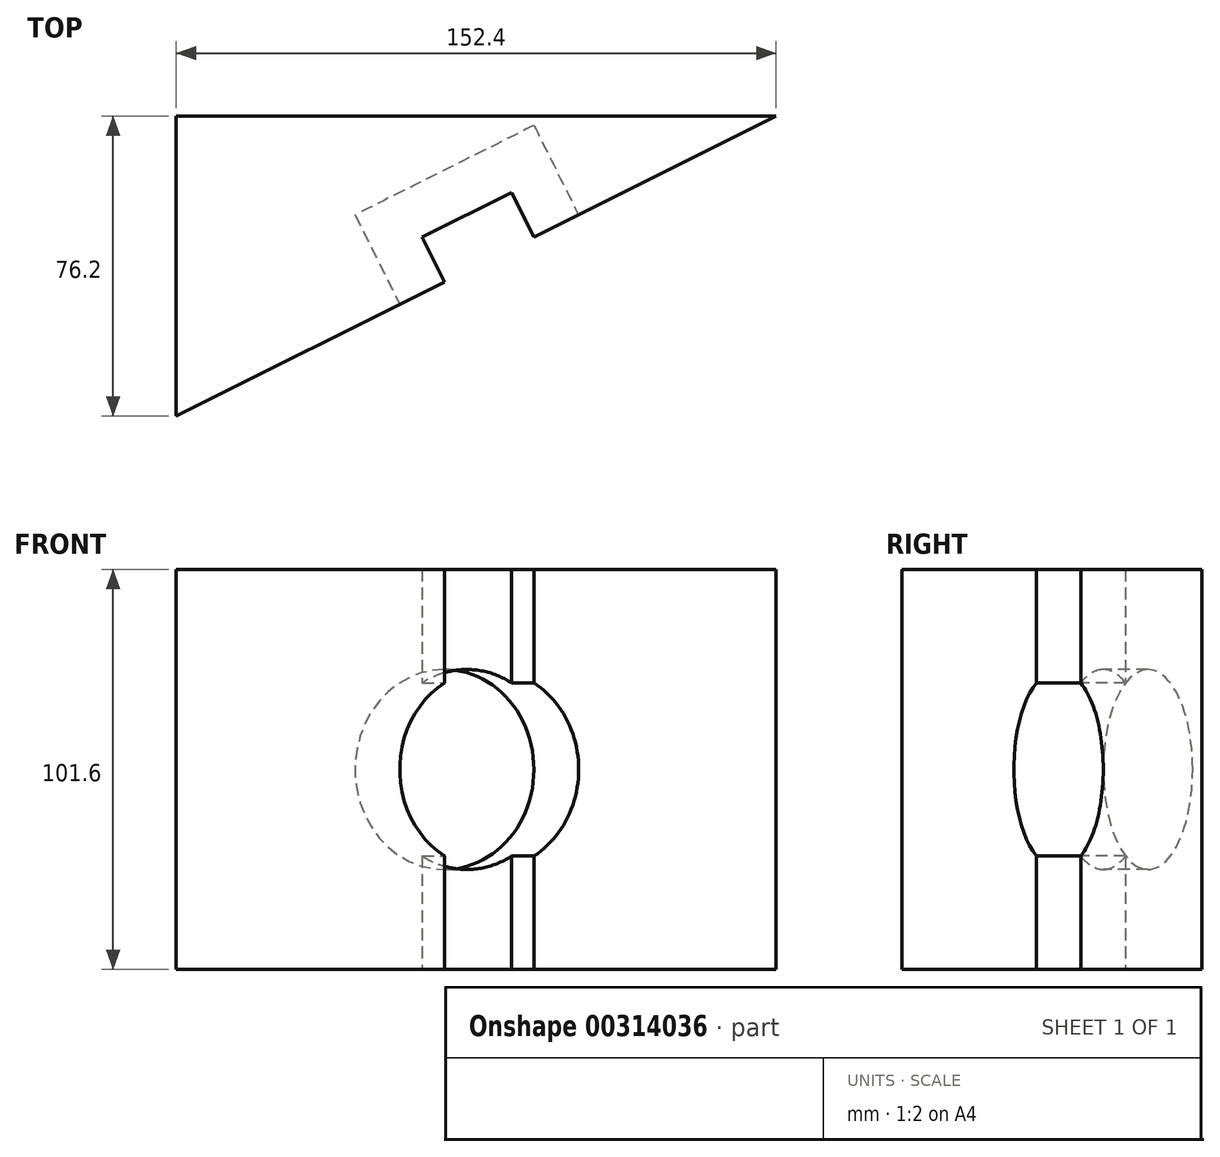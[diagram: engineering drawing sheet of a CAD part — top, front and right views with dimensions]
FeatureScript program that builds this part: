
annotation { "Feature Type Name" : "Feature", "Feature Type Description" : "" }
export const myFeature = defineFeature(function(context is Context, id is Id, definition is map)
    precondition{}
    {
        {
            var Q0;
            Q0=qCreatedBy(makeId("Top.planeOp"),FACE);
            var sketch = newSketch(context, id + "F0", { "sketchPlane" : qUnion([Q0])});
            skLineSegment(sketch, "E0.bottom", {"start": v(0, 0) * mm, "end": v(152.4, 0) * mm});
            skLineSegment(sketch, "E0.top", {"start": v(0, -76.2) * mm, "end": v(152.4, -76.2) * mm});
            skLineSegment(sketch, "E0.left", {"start": v(0, 0) * mm, "end": v(0, -76.2) * mm});
            skLineSegment(sketch, "E0.right", {"start": v(152.4, 0) * mm, "end": v(152.4, -76.2) * mm});
            skLineSegment(sketch, "E1", {"start": v(152.4, 0) * mm, "end": v(0, -76.2) * mm});
            skSolve(sketch);
        }
        {
            var Q0;
            Q0=makeQuery(id+"F0.imprint","IMPRINT",FACE,{"disambiguationData":[TD([[makeQuery(id+"F0.imprint","IMPRINT",EDGE,{"derivedFrom":sQuery(id+"F0.wireOp",EDGE,"E0.bottom")}),-1.0]])]});
            extrude(context, id + "F1", {"entities" : qUnion([Q0]), "depth" : 101.6 * mm});
        }
        {
            var Q0;
            Q0=makeQuery(id+"F1.opExtrude","SWEPT_FACE",FACE,{"disambiguationData":[OSD([sQuery(id+"F0.wireOp",EDGE,"E1")])]});
            var sketch = newSketch(context, id + "F2", { "sketchPlane" : qUnion([Q0])});
            skLineSegment(sketch, "E2.bottom", {"start": v(67.52, 101.6) * mm, "end": v(42.12, 101.6) * mm});
            skLineSegment(sketch, "E2.top", {"start": v(67.52, 0) * mm, "end": v(42.12, 0) * mm});
            skLineSegment(sketch, "E2.left", {"start": v(67.52, 101.6) * mm, "end": v(67.52, 0) * mm});
            skLineSegment(sketch, "E2.right", {"start": v(42.12, 101.6) * mm, "end": v(42.12, 0) * mm});
            skPoint(sketch, "E2.middle", {"position": v(54.82, 50.8) * mm});
            skSolve(sketch);
        }
        {
            var Q0;
            Q0=makeQuery(id+"F2.imprint","IMPRINT",FACE,{"disambiguationData":[TD([[makeQuery(id+"F2.imprint","IMPRINT",EDGE,{"derivedFrom":sQuery(id+"F2.wireOp",EDGE,"E2.bottom")}),1.0]])]});
            extrude(context, id + "F3", {"entities" : qUnion([Q0]), "operationType" : NewBodyOperationType.REMOVE, "oppositeDirection" : true, "depth" : 12.7 * mm});
        }
        {
            var Q0;
            {var subQ0=sQuery(id+"F0.wireOp",EDGE,"E0.bottom");var subQ1=sQuery(id+"F0.wireOp",EDGE,"E1");Q0=makeQuery(id+"F3.boolean.opBoolean","SPLIT",FACE,{"disambiguationData":[TD([makeQuery(id+"F1.opExtrude","SWEPT_FACE",FACE,{"disambiguationData":[OSD([subQ0])]})])],"derivedFrom":makeQuery(id+"F1.opExtrude","SWEPT_FACE",FACE,{"disambiguationData":[OSD([subQ1])]})});}
            var sketch = newSketch(context, id + "F4", { "sketchPlane" : qUnion([Q0])});
            skCircle(sketch, "E3", {"center": v(54.82, 50.8) * mm, "radius": 25.4 * mm});
            skSolve(sketch);
        }
        {
            var Q0;
            {var subQ0=sQuery(id+"F4.wireOp",EDGE,"E3");var subQ1=makeQuery(id+"F3.boolean.opBoolean","COPY",EDGE,{"derivedFrom":makeQuery(id+"F3.opExtrude","CAP_EDGE",EDGE,{"disambiguationData":[OSD([sQuery(id+"F2.wireOp",EDGE,"E2.left")])],"isStart":true})});var subQ2=makeQuery(id+"F4.imprint","INTERSECT",VERTEX,{"disambiguationData":[OD(0.0)],"derivedFrom":[subQ1,subQ0]});Q0=makeQuery(id+"F4.imprint","IMPRINT",FACE,{"disambiguationData":[TD([[makeQuery(id+"F4.imprint","IMPRINT",EDGE,{"disambiguationData":[TD([[subQ2,1.0]])],"derivedFrom":subQ0}),1.0]])]});}
            var Q1;
            {var subQ0=sQuery(id+"F4.wireOp",EDGE,"E3");var subQ1=makeQuery(id+"F3.boolean.opBoolean","COPY",EDGE,{"derivedFrom":makeQuery(id+"F3.opExtrude","CAP_EDGE",EDGE,{"disambiguationData":[OSD([sQuery(id+"F2.wireOp",EDGE,"E2.left")])],"isStart":true})});var subQ2=makeQuery(id+"F4.imprint","INTERSECT",VERTEX,{"disambiguationData":[OD(0.0)],"derivedFrom":[subQ1,subQ0]});Q1=makeQuery(id+"F4.imprint","IMPRINT",FACE,{"disambiguationData":[TD([[makeQuery(id+"F4.imprint","IMPRINT",EDGE,{"disambiguationData":[TD([[subQ2,-1.0]])],"derivedFrom":subQ0}),1.0]])]});}
            extrude(context, id + "F5", {"entities" : qUnion([Q0, Q1]), "operationType" : NewBodyOperationType.REMOVE, "oppositeDirection" : true, "depth" : 25.4 * mm});
        }
    });
